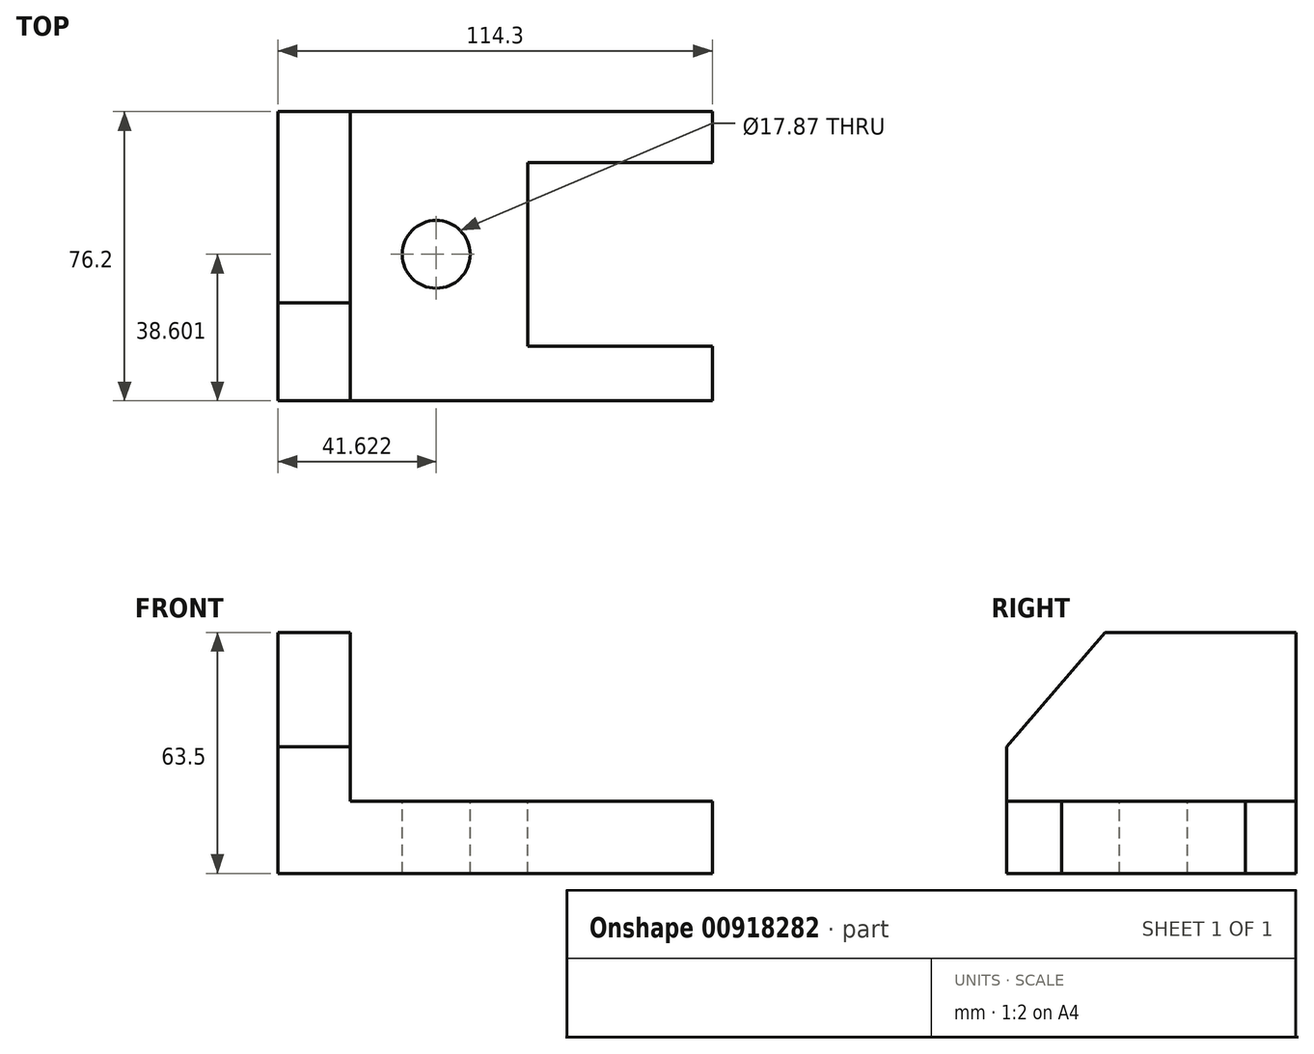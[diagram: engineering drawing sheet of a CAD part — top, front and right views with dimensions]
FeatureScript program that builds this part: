
annotation { "Feature Type Name" : "Feature", "Feature Type Description" : "" }
export const myFeature = defineFeature(function(context is Context, id is Id, definition is map)
    precondition{}
    {
        {
            var Q0;
            Q0=qCreatedBy(makeId("Front.planeOp"),FACE);
            var sketch = newSketch(context, id + "F0", { "sketchPlane" : qUnion([Q0])});
            skLineSegment(sketch, "E0", {"start": v(-49.06, 30.12) * mm, "end": v(-49.06, -33.38) * mm});
            skLineSegment(sketch, "E1", {"start": v(-49.06, -33.38) * mm, "end": v(65.24, -33.38) * mm});
            skLineSegment(sketch, "E2", {"start": v(-49.06, 30.12) * mm, "end": v(-30, 30.12) * mm});
            skLineSegment(sketch, "E3", {"start": v(65.24, -33.38) * mm, "end": v(65.24, -14.33) * mm});
            skLineSegment(sketch, "E4", {"start": v(65.24, -14.33) * mm, "end": v(-30, -14.33) * mm});
            skLineSegment(sketch, "E5", {"start": v(-30, -14.33) * mm, "end": v(-30, 30.12) * mm});
            skSolve(sketch);
        }
        {
            var Q0;
            Q0=makeQuery(id+"F0.imprint","IMPRINT",FACE,{"disambiguationData":[TD([[makeQuery(id+"F0.imprint","IMPRINT",EDGE,{"derivedFrom":sQuery(id+"F0.wireOp",EDGE,"E0")}),1.0]])]});
            extrude(context, id + "F1", {"entities" : qUnion([Q0]), "depth" : 76.2 * mm, "offsetDistance" : 25.4 * mm});
        }
        {
            var Q0;
            Q0=makeQuery(id+"F1.opExtrude","SWEPT_FACE",FACE,{"disambiguationData":[OSD([sQuery(id+"F0.wireOp",EDGE,"E0")])]});
            var sketch = newSketch(context, id + "F2", { "sketchPlane" : qUnion([Q0])});
            skLineSegment(sketch, "E6", {"start": v(0, 30.12) * mm, "end": v(50.35, 30.12) * mm});
            skLineSegment(sketch, "E7", {"start": v(50.35, 30.12) * mm, "end": v(50.35, 0) * mm});
            skLineSegment(sketch, "E8", {"start": v(50.35, 0) * mm, "end": v(76.2, 0) * mm});
            skLineSegment(sketch, "E9", {"start": v(76.2, 0) * mm, "end": v(50.35, 30.12) * mm});
            skSolve(sketch);
        }
        {
            var Q0;
            {var subQ0=sQuery(id+"F2.wireOp",EDGE,"E9");Q0=makeQuery(id+"F2.imprint","IMPRINT",FACE,{"disambiguationData":[TD([[makeQuery(id+"F2.imprint","IMPRINT",EDGE,{"derivedFrom":subQ0}),-1.0]])]});}
            var sketch = newSketch(context, id + "F3", { "sketchPlane" : qUnion([Q0])});
            skSolve(sketch);
        }
        {
            var Q0;
            Q0 = qSketchRegion(id + "F3", true);
            var Q1;
            {var subQ0=sQuery(id+"F2.wireOp",EDGE,"E9");Q1=makeQuery(id+"F3.imprint","IMPRINT",FACE,{"disambiguationData":[TD([[makeQuery(id+"F3.imprint","IMPRINT",EDGE,{"derivedFrom":makeQuery(id+"F2.imprint","IMPRINT",EDGE,{"derivedFrom":subQ0})}),-1.0]])]});}
            extrude(context, id + "F4", {"entities" : qUnion([Q0, Q1]), "operationType" : NewBodyOperationType.REMOVE, "endBound" : BoundingType.THROUGH_ALL, "oppositeDirection" : true, "depth" : 25.4 * mm, "offsetDistance" : 25.4 * mm});
        }
        {
            var Q0;
            {var subQ0=sQuery(id+"F2.wireOp",EDGE,"E9");Q0=makeQuery(id+"F2.imprint","IMPRINT",FACE,{"disambiguationData":[TD([[makeQuery(id+"F2.imprint","IMPRINT",EDGE,{"derivedFrom":subQ0}),-1.0]])]});}
            extrude(context, id + "F5", {"entities" : qUnion([Q0]), "operationType" : NewBodyOperationType.REMOVE, "endBound" : BoundingType.THROUGH_ALL, "oppositeDirection" : true, "depth" : 25.4 * mm, "offsetDistance" : 25.4 * mm});
        }
        {
            var Q0;
            Q0=makeQuery(id+"F1.opExtrude","SWEPT_FACE",FACE,{"disambiguationData":[OSD([sQuery(id+"F0.wireOp",EDGE,"E4")])]});
            var sketch = newSketch(context, id + "F6", { "sketchPlane" : qUnion([Q0])});
            skLineSegment(sketch, "E10", {"start": v(65.24, -38.1) * mm, "end": v(16.7, -38.1) * mm});
            skLineSegment(sketch, "E11", {"start": v(16.7, -38.1) * mm, "end": v(16.7, -13.39) * mm});
            skLineSegment(sketch, "E12", {"start": v(16.7, -13.39) * mm, "end": v(65.24, -13.39) * mm});
            skLineSegment(sketch, "E13", {"start": v(16.7, -38.1) * mm, "end": v(16.7, -61.81) * mm});
            skLineSegment(sketch, "E14", {"start": v(16.7, -61.81) * mm, "end": v(65.24, -61.81) * mm});
            skSolve(sketch);
        }
        {
            var Q0;
            {var subQ0=sQuery(id+"F6.wireOp",EDGE,"E10");Q0=makeQuery(id+"F6.imprint","IMPRINT",FACE,{"disambiguationData":[TD([[makeQuery(id+"F6.imprint","IMPRINT",EDGE,{"derivedFrom":subQ0}),1.0]])]});}
            var Q1;
            {var subQ0=sQuery(id+"F6.wireOp",EDGE,"E10");Q1=makeQuery(id+"F6.imprint","IMPRINT",FACE,{"disambiguationData":[TD([[makeQuery(id+"F6.imprint","IMPRINT",EDGE,{"derivedFrom":subQ0}),-1.0]])]});}
            extrude(context, id + "F7", {"entities" : qUnion([Q0, Q1]), "operationType" : NewBodyOperationType.REMOVE, "endBound" : BoundingType.THROUGH_ALL, "oppositeDirection" : true, "depth" : 25.4 * mm, "offsetDistance" : 25.4 * mm});
        }
        {
            var Q0;
            Q0=makeQuery(id+"F1.opExtrude","SWEPT_FACE",FACE,{"disambiguationData":[OSD([sQuery(id+"F0.wireOp",EDGE,"E4")])]});
            var sketch = newSketch(context, id + "F8", { "sketchPlane" : qUnion([Q0])});
            skCircle(sketch, "E15", {"center": v(-7.44, -37.6) * mm, "radius": 8.94 * mm});
            skPoint(sketch, "E15.centerSnap0", {"position": v(16.7, -37.6) * mm});
            skSolve(sketch);
        }
        {
            var Q0;
            Q0=makeQuery(id+"F8.imprint","IMPRINT",FACE,{"disambiguationData":[TD([[makeQuery(id+"F8.imprint","IMPRINT",EDGE,{"derivedFrom":sQuery(id+"F8.wireOp",EDGE,"E15")}),1.0]])]});
            extrude(context, id + "F9", {"entities" : qUnion([Q0]), "operationType" : NewBodyOperationType.REMOVE, "endBound" : BoundingType.THROUGH_ALL, "oppositeDirection" : true, "depth" : 25.4 * mm, "offsetDistance" : 25.4 * mm});
        }
    });
